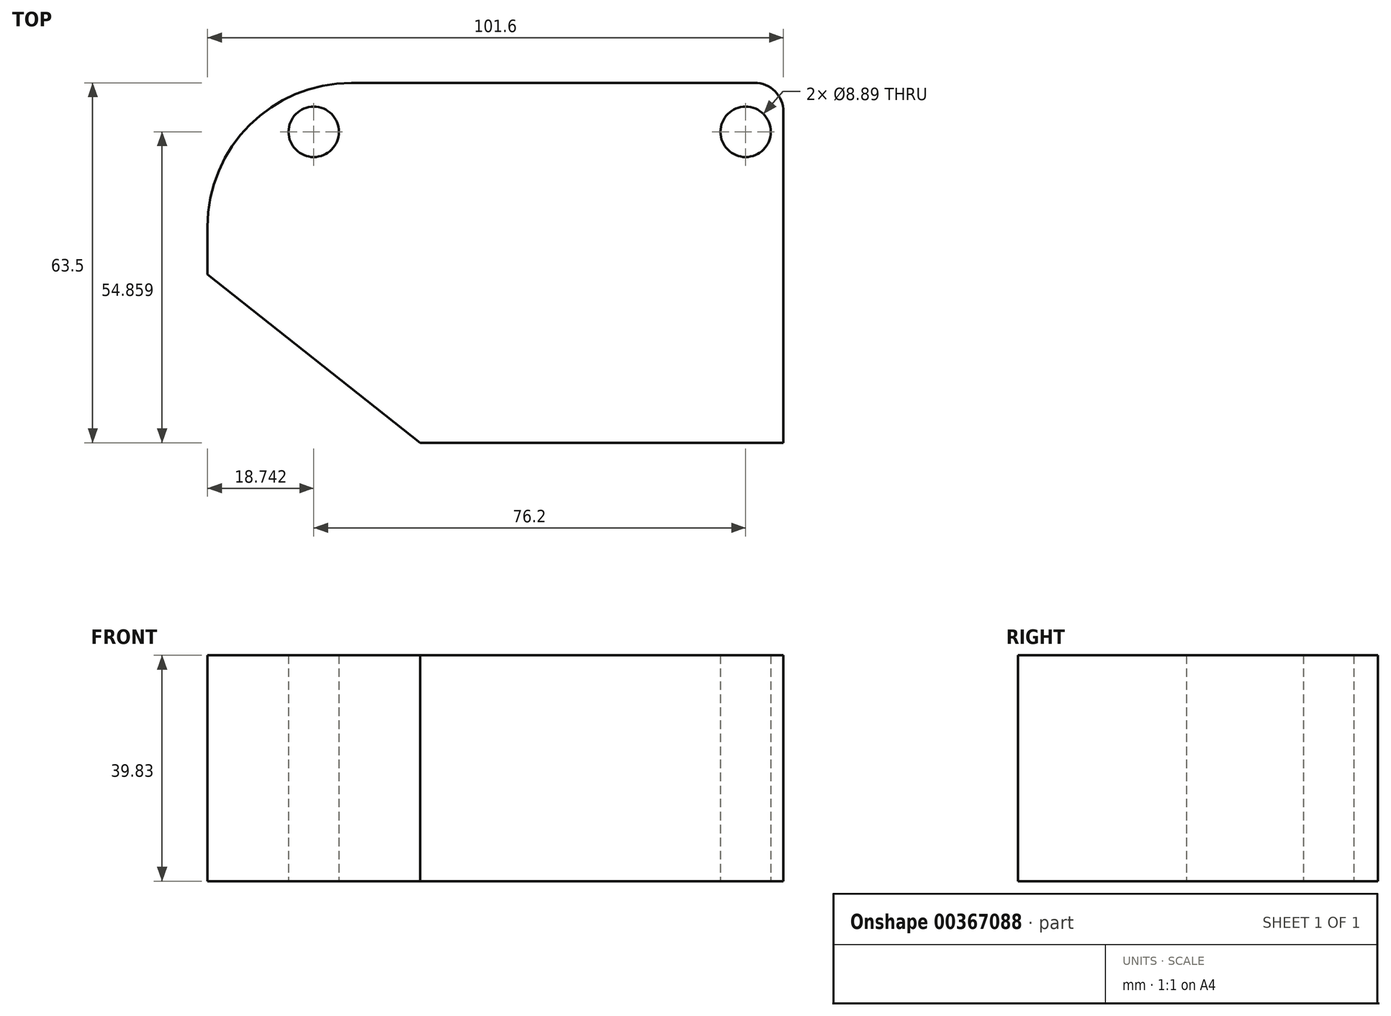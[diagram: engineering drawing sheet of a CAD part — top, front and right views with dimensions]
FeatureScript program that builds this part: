
annotation { "Feature Type Name" : "Feature", "Feature Type Description" : "" }
export const myFeature = defineFeature(function(context is Context, id is Id, definition is map)
    precondition{}
    {
        {
            var Q0;
            Q0=qCreatedBy(makeId("Front.planeOp"),FACE);
            var sketch = newSketch(context, id + "F0", { "sketchPlane" : qUnion([Q0])});
            skLineSegment(sketch, "E0.bottom", {"start": v(0, 0) * mm, "end": v(-101.6, 0) * mm});
            skLineSegment(sketch, "E0.top", {"start": v(0, -39.83) * mm, "end": v(-101.6, -39.83) * mm});
            skLineSegment(sketch, "E0.left", {"start": v(0, 0) * mm, "end": v(0, -39.83) * mm});
            skLineSegment(sketch, "E0.right", {"start": v(-101.6, 0) * mm, "end": v(-101.6, -39.83) * mm});
            skSolve(sketch);
        }
        {
            var Q0;
            Q0=makeQuery(id+"F0.imprint","IMPRINT",FACE,{"disambiguationData":[TD([[makeQuery(id+"F0.imprint","IMPRINT",EDGE,{"derivedFrom":sQuery(id+"F0.wireOp",EDGE,"E0.bottom")}),1.0]])]});
            extrude(context, id + "F1", {"entities" : qUnion([Q0]), "depth" : 63.5 * mm});
        }
        {
            var Q0;
            Q0=makeQuery(id+"F1.opExtrude","SWEPT_FACE",FACE,{"disambiguationData":[OSD([sQuery(id+"F0.wireOp",EDGE,"E0.top")])]});
            var sketch = newSketch(context, id + "F2", { "sketchPlane" : qUnion([Q0])});
            skLineSegment(sketch, "E1", {"start": v(-101.6, 33.76) * mm, "end": v(-64.07, 63.5) * mm});
            skSolve(sketch);
        }
        {
            var Q0;
            {var subQ0=sQuery(id+"F2.wireOp",EDGE,"E1");Q0=makeQuery(id+"F2.imprint","IMPRINT",FACE,{"disambiguationData":[TD([[makeQuery(id+"F2.imprint","IMPRINT",EDGE,{"derivedFrom":subQ0}),1.0]])]});}
            extrude(context, id + "F3", {"entities" : qUnion([Q0]), "operationType" : NewBodyOperationType.REMOVE, "oppositeDirection" : true, "depth" : 106.68 * mm});
        }
        {
            var Q0;
            Q0=makeQuery(id+"F3.boolean.opBoolean","COPY",EDGE,{"derivedFrom":makeQuery(id+"F3.opExtrude","SWEPT_EDGE",EDGE,{"disambiguationData":[OSD([sQuery(id+"F0.wireOp",EDGE,"E0.top"),sQuery(id+"F0.wireOp",EDGE,"E0.right"),sQuery(id+"F2.wireOp",EDGE,"E1")])]})});
            var Q1;
            Q1=makeQuery(id+"F1.opExtrude","CAP_EDGE",EDGE,{"disambiguationData":[OSD([sQuery(id+"F0.wireOp",EDGE,"E0.right")])],"isStart":true});
            fillet(context, id + "F4", {"entities" : qUnion([Q0, Q1]), "radius" : 25.4 * mm, "tangentPropagation" : true, "allowEdgeOverflow" : false});
        }
        {
            var Q0;
            Q0=makeQuery(id+"F1.opExtrude","CAP_EDGE",EDGE,{"disambiguationData":[OSD([sQuery(id+"F0.wireOp",EDGE,"E0.left")])],"isStart":true});
            fillet(context, id + "F5", {"entities" : qUnion([Q0]), "radius" : 5.08 * mm, "tangentPropagation" : true, "allowEdgeOverflow" : false});
        }
        {
            var Q0;
            Q0=makeQuery(id+"F1.opExtrude","SWEPT_FACE",FACE,{"disambiguationData":[OSD([sQuery(id+"F0.wireOp",EDGE,"E0.top")])]});
            var sketch = newSketch(context, id + "F6", { "sketchPlane" : qUnion([Q0])});
            skCircle(sketch, "E2", {"center": v(-82.86, 8.64) * mm, "radius": 4.45 * mm});
            skCircle(sketch, "E3", {"center": v(-6.66, 8.64) * mm, "radius": 4.45 * mm});
            skSolve(sketch);
        }
        {
            var Q0;
            Q0=makeQuery(id+"F6.imprint","IMPRINT",FACE,{"disambiguationData":[TD([[makeQuery(id+"F6.imprint","IMPRINT",EDGE,{"derivedFrom":sQuery(id+"F6.wireOp",EDGE,"E2")}),1.0]])]});
            var Q1;
            Q1=makeQuery(id+"F6.imprint","IMPRINT",FACE,{"disambiguationData":[TD([[makeQuery(id+"F6.imprint","IMPRINT",EDGE,{"derivedFrom":sQuery(id+"F6.wireOp",EDGE,"E3")}),1.0]])]});
            extrude(context, id + "F7", {"entities" : qUnion([Q0, Q1]), "operationType" : NewBodyOperationType.REMOVE, "oppositeDirection" : true, "depth" : 50.8 * mm});
        }
    });
